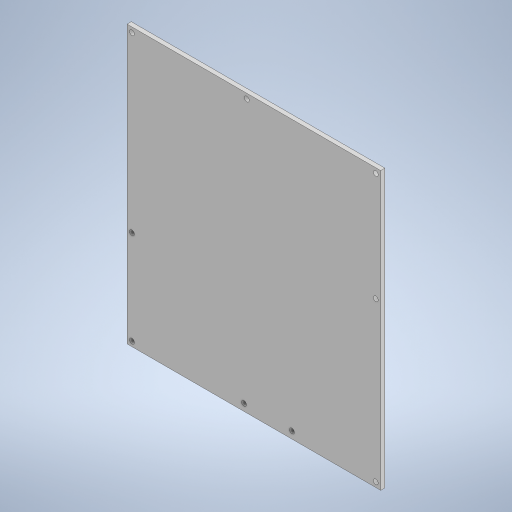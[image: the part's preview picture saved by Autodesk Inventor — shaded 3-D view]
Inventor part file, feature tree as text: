
AUTODESK INVENTOR PART (.ipt)
format: ipt  version: 2023 (Build 270158000, 158)  size: 228,352 bytes
history: native  units: in
note: dims shown in document units (in); Inventor stores cm internally (conversion verified against a paired STEP export)
features: sketch x2, extrude x1, hole x1, projected_geometry x1
ambient origin geometry x8: Origin, YZ Plane, XZ Plane, XY Plane, X Axis, Y Axis, Z Axis, Center Point
bodies: Solid1 (feature_tree)
feature tree (5):
  extrude  "Extrusion1"  Depth=7.7362in
  hole  "Hole1"  [1 undecoded]
  sketch  "Sketch1"  dims[d9=7.0866in d15=7.7362in]
  sketch  "Sketch2"  dims[d18=0.1181in d19=0.0in d21=0.1378in d22=3.3465in d23=4.5669in d26=2.7559in d27=0.1339in d28=0.2362in d29=0.1575in d30=0.0787in d31=90.0deg d32=0.315in d33=0.8108in d34=0.1969in d35=4.6063in d36=3.2681in]
  projected_geometry  "Projected Loop1"
note: 1 required parameter value undecoded (feature->parameter linkage not recoverable at this tier; creation-order binding heuristic only, values carry confidence <= 0.55)
